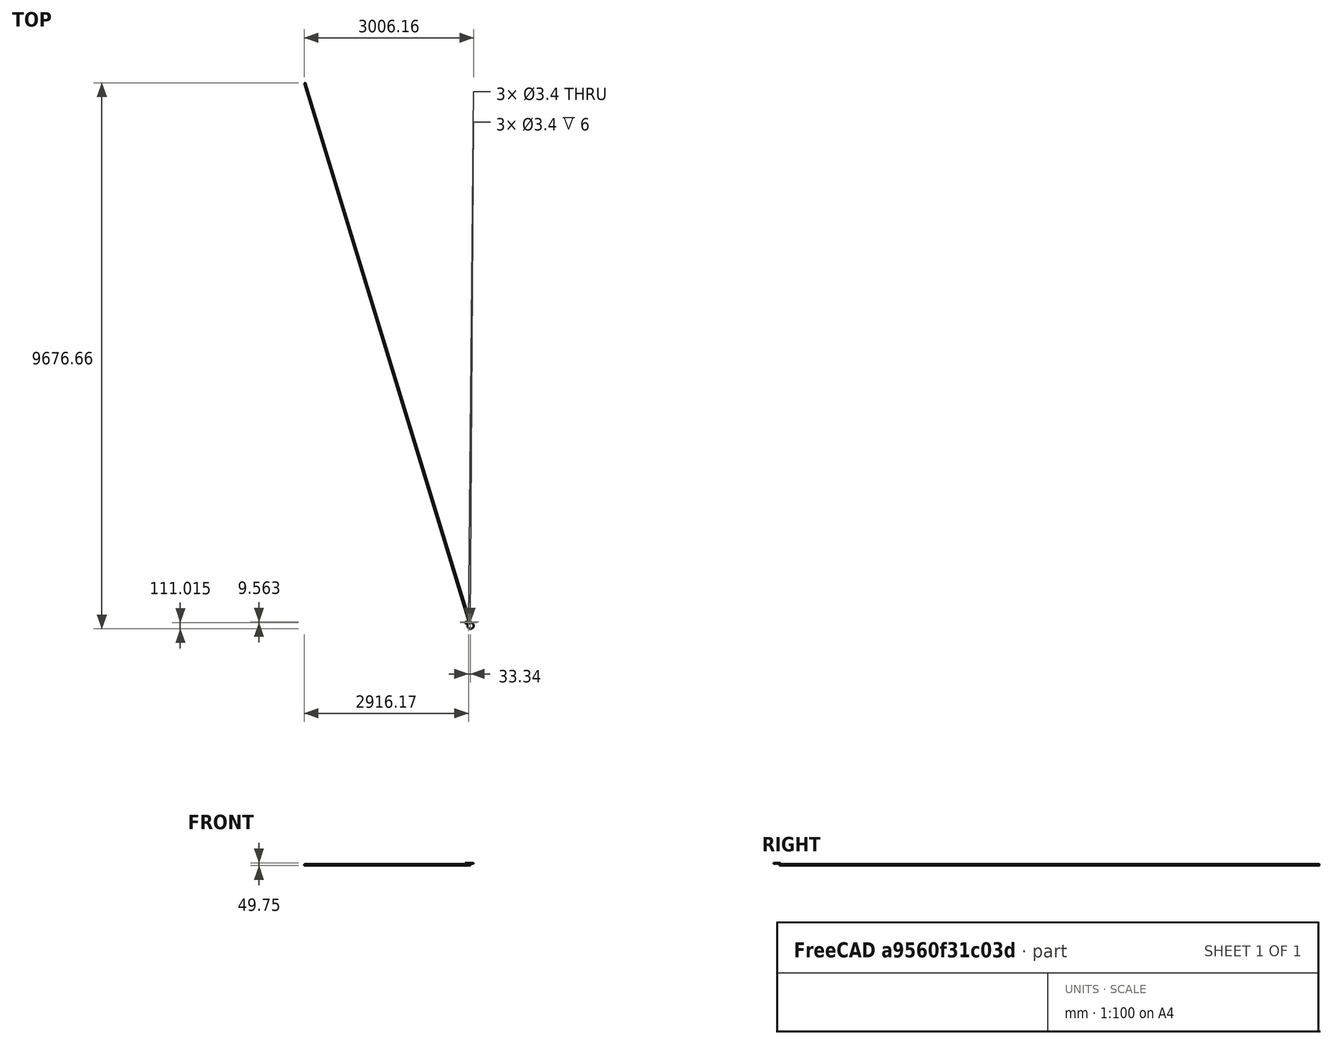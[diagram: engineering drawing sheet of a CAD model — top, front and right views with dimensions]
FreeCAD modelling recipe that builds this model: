
FCSTD DOCUMENT  (FreeCAD 0.16R)
Label: Guide9
License: All rights reserved
LicenseURL: http://en.wikipedia.org/wiki/All_rights_reserved
objects: Sketcher::SketchObject×9, PartDesign::Pocket×7, PartDesign::Fillet×4, PartDesign::Chamfer×3, PartDesign::Pad×2, Mesh::Feature×1
note: 34 computed .brp shape members not serialized (recipe doc carries the construction recipe); baked Part::Feature solids carry a one-line shape summary decoded from their .brp

FEATURE [Sketcher::SketchObject] Sketch
  sketch-geometry (4):
    g0: LineSegment StartX=-50 StartY=0 StartZ=0 EndX=0 EndY=0 EndZ=0
    g1: LineSegment StartX=0 StartY=0 StartZ=0 EndX=0 EndY=-30 EndZ=0
    g2: LineSegment StartX=0 StartY=-30 StartZ=0 EndX=-50 EndY=-30 EndZ=0
    g3: LineSegment StartX=-50 StartY=-30 StartZ=0 EndX=-50 EndY=0 EndZ=0
  constraints (11):
    c: Coincident(g0,g1)
    c: Coincident(g1,g2)
    c: Coincident(g2,g3)
    c: Coincident(g3,g0)
    c: Horizontal(g0)
    c: Horizontal(g2)
    c: Vertical(g1)
    c: Vertical(g3)
    c: Coincident(g0,g-1)
    c: Distance(g3) = 30
    c: Distance(g0) = 50
FEATURE [PartDesign::Pad] Pad
  Length = 12
  Length2 = 100
  Midplane = true
  Sketch = -> Sketch
  Type = 0
FEATURE [Sketcher::SketchObject] Sketch001
  Placement = pos=(0,-30,0) rot=(1,0,0;1.5708rad)
  Support = -> Pad [Face3]
  sketch-geometry (4):
    g0: LineSegment StartX=-95.8323 StartY=4.5 StartZ=0 EndX=18.8197 EndY=4.5 EndZ=0
    g1: LineSegment StartX=18.8197 StartY=4.5 StartZ=0 EndX=18.8197 EndY=-4.5 EndZ=0
    g2: LineSegment StartX=18.8197 StartY=-4.5 StartZ=0 EndX=-95.8323 EndY=-4.5 EndZ=0
    g3: LineSegment StartX=-95.8323 StartY=-4.5 StartZ=0 EndX=-95.8323 EndY=4.5 EndZ=0
  constraints (12):
    c: Coincident(g0,g1)
    c: Coincident(g1,g2)
    c: Coincident(g2,g3)
    c: Coincident(g3,g0)
    c: Horizontal(g0)
    c: Horizontal(g2)
    c: Vertical(g1)
    c: Vertical(g3)
    c: DistanceX(g1) = 18.8197
    c: DistanceX(g2) = -95.8323
    c: Symmetric(g1,g0,g-1)
    c: Distance(g1) = 9
FEATURE [PartDesign::Pocket] Pocket
  Length = 26
  Sketch = -> Sketch001
  Type = 0
FEATURE [Sketcher::SketchObject] Sketch003
  ExternalGeometry = -> [Pocket]
  Placement = pos=(0,0,-6) rot=(1,0,0;3.14159rad)
  Support = -> Pocket [Face4]
  sketch-geometry (7):
    g0: LineSegment StartX=-39.7363 StartY=0 StartZ=0 EndX=0 EndY=0 EndZ=0
    g1: LineSegment StartX=0 StartY=0 StartZ=0 EndX=2.92372 EndY=9.56305 EndZ=0
    g2: LineSegment StartX=2.92372 StartY=9.56305 StartZ=0 EndX=-33.4159 EndY=20.6732 EndZ=0
    g3: LineSegment StartX=-33.4159 StartY=20.6732 StartZ=0 EndX=-39.7363 EndY=0 EndZ=0
    g4: LineSegment [constr] StartX=-6.16153 StartY=44.8323 StartZ=0 EndX=-26.2639 EndY=-20.9195 EndZ=0
    g5: LineSegment StartX=-39.7363 StartY=0 StartZ=0 EndX=0 EndY=0 EndZ=0
    g6: LineSegment StartX=-39.7363 StartY=0 StartZ=0 EndX=0 EndY=0 EndZ=0
  constraints (21):
    c: Horizontal(g0)
    c: Coincident(g0,g1)
    c: Coincident(g1,g2)
    c: Coincident(g2,g3)
    c: Coincident(g3,g0)
    c: Parallel(g1,g3)
    c: Perpendicular(g3,g2)
    c: Distance(g2) = 38
    c: PointOnObject(g0,g-3)
    c: Perpendicular(g4,g2)
    c: Symmetric(g1,g2,g4)
    c: Distance(g1) = 10
    c: Angle(g4) = -1.8675
    c: DistanceX(g0) = 0
    c: Distance(g4) = 68.7561
    c: DistanceY(g4) = 44.8323
    c: Coincident(g5,g0)
    c: PointOnObject(g5,g-1)
    c: Coincident(g6,g0)
    c: Coincident(g6,g5)
    c: Coincident(g5,g0)
FEATURE [PartDesign::Pad] Pad001
  Length = 25
  Length2 = 100
  Sketch = -> Sketch003
  Type = 0
FEATURE [Sketcher::SketchObject] Sketch004
  ExternalGeometry = -> [Pad001]
  Placement = pos=(2.92372,-9.56305,0) rot=(0.978386,0.146221,0.146221;1.59265rad)
  Support = -> Pad001 [Face11]
  sketch-geometry (1):
    g0: Circle CenterX=-19 CenterY=-31 CenterZ=0 NormalX=0 NormalY=0 NormalZ=1 Radius=12.75
  constraints (2):
    c: Radius(g0) = 12.75
    c: Symmetric(g-3,g-3,g0)
FEATURE [PartDesign::Pocket] Pocket001
  Length = 5
  Sketch = -> Sketch004
  Type = 1
FEATURE [Sketcher::SketchObject] Sketch005
  Placement = pos=(0,0,6) rot=(0,0,1;0rad)
  Support = -> Pocket001 [Face4]
  sketch-geometry (1):
    g0: Circle CenterX=0 CenterY=-70 CenterZ=0 NormalX=0 NormalY=0 NormalZ=1 Radius=55
  constraints (3):
    c: Radius(g0) = 55
    c: PointOnObject(g0,g-2)
    c: DistanceY(g0) = -70
FEATURE [PartDesign::Pocket] Pocket002
  Length = 13
  Sketch = -> Sketch005
  Type = 0
FEATURE [Sketcher::SketchObject] Sketch007
  ExternalGeometry = -> [Pocket002]
  Placement = pos=(-36.3396,-11.1101,0) rot=(0.690875,-0.51122,-0.51122;1.93244rad)
  Support = -> Pocket002 [Face13]
  sketch-geometry (9):
    g0: LineSegment StartX=1.2 StartY=-22 StartZ=0 EndX=7 EndY=-22 EndZ=0
    g1: LineSegment StartX=7 StartY=-22 StartZ=0 EndX=7 EndY=-25 EndZ=0
    g2: LineSegment StartX=7 StartY=-25 StartZ=0 EndX=1.2 EndY=-25 EndZ=0
    g3: LineSegment StartX=1.2 StartY=-25 StartZ=0 EndX=1.2 EndY=-22 EndZ=0
    g4: LineSegment [constr] StartX=4.1 StartY=-22 StartZ=0 EndX=4.1 EndY=-31 EndZ=0
    g5: LineSegment StartX=-8.8 StartY=-22 StartZ=0 EndX=-3 EndY=-22 EndZ=0
    g6: LineSegment StartX=-3 StartY=-22 StartZ=0 EndX=-3 EndY=-25 EndZ=0
    g7: LineSegment StartX=-3 StartY=-25 StartZ=0 EndX=-8.8 EndY=-25 EndZ=0
    g8: LineSegment StartX=-8.8 StartY=-25 StartZ=0 EndX=-8.8 EndY=-22 EndZ=0
  constraints (28):
    c: Coincident(g0,g1)
    c: Coincident(g1,g2)
    c: Coincident(g2,g3)
    c: Coincident(g3,g0)
    c: Horizontal(g0)
    c: Horizontal(g2)
    c: Vertical(g1)
    c: Vertical(g3)
    c: Distance(g2) = 5.8
    c: Distance(g1) = 3
    c: Vertical(g4)
    c: Symmetric(g0,g0,g4)
    c: PointOnObject(g4,g0)
    c: Distance(g1,g-3) = 3
    c: Distance(g1,g-4) = 6
    c: Coincident(g5,g6)
    c: Coincident(g6,g7)
    c: Coincident(g7,g8)
    c: Coincident(g8,g5)
    c: Horizontal(g5)
    c: Horizontal(g7)
    c: Vertical(g6)
    c: Vertical(g8)
    c: Distance(g6) = 3
    c: Distance(g7) = 5.8
    c: Distance(g6,g-4) = 6
    c: Distance(g6,g1) = 10
    c: PointOnObject(g4,g-4)
FEATURE [PartDesign::Pocket] Pocket003
  Length = 6
  Sketch = -> Sketch007
  Type = 0
FEATURE [Sketcher::SketchObject] Sketch008
  ExternalGeometry = -> [Pocket003]
  Placement = pos=(0,0,0) rot=(0.463605,0.626526,0.626526;2.27337rad)
  Support = -> Pocket003 [Face20]
  sketch-geometry (5):
    g0: LineSegment StartX=-8 StartY=-22 StartZ=0 EndX=-2 EndY=-22 EndZ=0
    g1: LineSegment StartX=-2 StartY=-22 StartZ=0 EndX=-2 EndY=-25 EndZ=0
    g2: LineSegment StartX=-2 StartY=-25 StartZ=0 EndX=-8 EndY=-25 EndZ=0
    g3: LineSegment StartX=-8 StartY=-25 StartZ=0 EndX=-8 EndY=-22 EndZ=0
    g4: LineSegment [constr] StartX=-5 StartY=-22 StartZ=0 EndX=-5 EndY=-31 EndZ=0
  constraints (16):
    c: Coincident(g0,g1)
    c: Coincident(g1,g2)
    c: Coincident(g2,g3)
    c: Coincident(g3,g0)
    c: Horizontal(g0)
    c: Horizontal(g2)
    c: Vertical(g1)
    c: Vertical(g3)
    c: Distance(g2) = 6
    c: Distance(g1) = 3
    c: Vertical(g4)
    c: Symmetric(g0,g0,g4)
    c: PointOnObject(g4,g0)
    c: Distance(g0,g-3) = 2
    c: Distance(g1,g-4) = 6
    c: PointOnObject(g4,g-4)
FEATURE [PartDesign::Pocket] Pocket004
  Length = 6
  Sketch = -> Sketch008
  Type = 0
FEATURE [Sketcher::SketchObject] Sketch006
  ExternalGeometry = -> [Pocket004]
  Placement = pos=(0,0,-31) rot=(1,0,0;3.14159rad)
  Support = -> Pocket004 [Face17]
  sketch-geometry (3):
    g0: Circle CenterX=-32.0621 CenterY=13.9851 CenterZ=0 NormalX=0 NormalY=0 NormalZ=1 Radius=1.7
    g1: Circle CenterX=-1.64613 CenterY=5.73173 CenterZ=0 NormalX=0 NormalY=0 NormalZ=1 Radius=1.7
    g2: Circle CenterX=-34.9858 CenterY=4.42209 CenterZ=0 NormalX=0 NormalY=0 NormalZ=1 Radius=1.7
  constraints (9):
    c: Radius(g1) = 1.7
    c: Equal(g1,g0)
    c: Distance(g0,g-4) = 3
    c: Distance(g0,g-3) = 6
    c: Distance(g1,g-6) = 3
    c: Distance(g1,g-5) = 5
    c: Distance(g2,g0) = 10
    c: Distance(g2,g-4) = 3
    c: Radius(g2) = 1.7
FEATURE [PartDesign::Pocket] Pocket005
  Length = 15
  Sketch = -> Sketch006
  Type = 0
FEATURE [Sketcher::SketchObject] Sketch009
  ExternalGeometry = -> [Pocket005]
  Placement = pos=(0,0,-6) rot=(1,0,0;3.14159rad)
  Support = -> Pocket005 [Face2]
  sketch-geometry (3):
    g0: ArcOfCircle CenterX=-3.87718 CenterY=-19.3051 CenterZ=0 NormalX=0 NormalY=0 NormalZ=1 Radius=50 StartAngle=1.90839 EndAngle=2.74519
    g1: LineSegment StartX=-20.4383 StartY=27.8726 StartZ=0 EndX=-66.5611 EndY=47.1776 EndZ=0
    g2: LineSegment StartX=-66.5611 StartY=47.1776 StartZ=0 EndX=-50 EndY=0 EndZ=0
  constraints (9):
    c: Radius(g0) = 50
    c: Coincident(g0,g-4)
    c: DistanceX(g0) = -3.87718
    c: Coincident(g1,g2)
    c: Coincident(g2,g0)
    c: Distance(g2) = 50
    c: Distance(g1) = 50
    c: DistanceX(g1) = -66.5611
    c: Coincident(g0,g1)
FEATURE [PartDesign::Pocket] Pocket006
  Length = 10.5
  Sketch = -> Sketch009
  Type = 1
FEATURE [PartDesign::Fillet] Fillet
  Base = -> Pocket006 [Edge1]
  Radius = 2
FEATURE [PartDesign::Fillet] Fillet001
  Base = -> Fillet [Edge40,Edge38,Edge23,Edge27]
  Radius = 4
FEATURE [PartDesign::Chamfer] Chamfer
  Base = -> Fillet001 [Edge24]
  Size = 1
FEATURE [PartDesign::Chamfer] Chamfer001
  Base = -> Chamfer [Edge72,Edge51]
  Size = 1
FEATURE [PartDesign::Chamfer] Chamfer002
  Base = -> Chamfer001 [Edge35]
  Size = 1
FEATURE [PartDesign::Fillet] Fillet002
  Base = -> Chamfer002 [Edge62]
  Radius = 1
FEATURE [PartDesign::Fillet] Fillet003
  Base = -> Fillet002 [Edge9]
  Radius = 1
FEATURE [Mesh::Feature] Mesh  label="Fillet003 (Meshed)"
